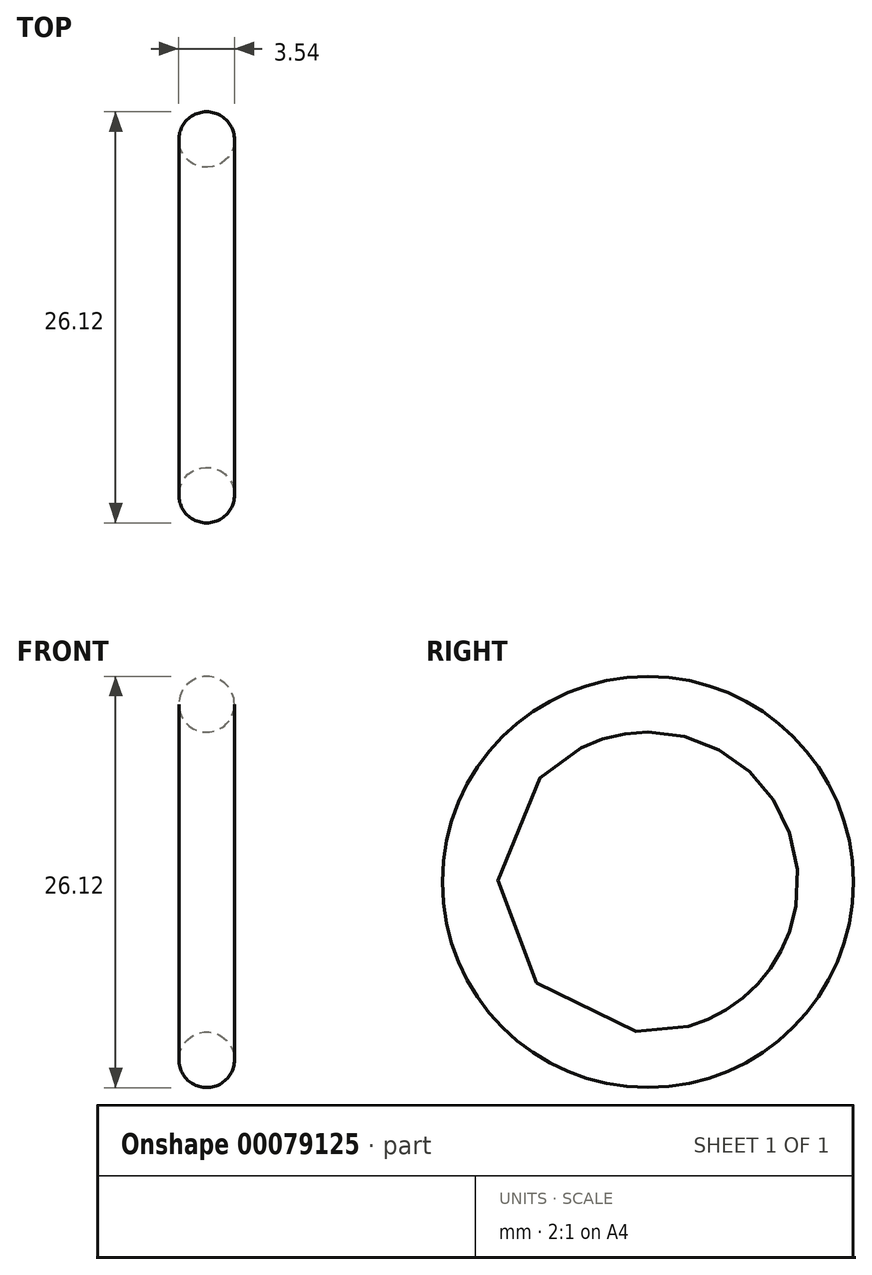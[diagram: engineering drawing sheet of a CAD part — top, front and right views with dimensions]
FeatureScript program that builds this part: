
annotation { "Feature Type Name" : "Feature", "Feature Type Description" : "" }
export const myFeature = defineFeature(function(context is Context, id is Id, definition is map)
    precondition{}
    {
        {
            var Q0;
            Q0=qCreatedBy(makeId("Front.planeOp"),FACE);
            var sketch = newSketch(context, id + "F0", { "sketchPlane" : qUnion([Q0])});
            skLineSegment(sketch, "E0", {"start": v(-17.65, 0) * mm, "end": v(27.96, 0) * mm});
            skCircle(sketch, "E1", {"center": v(0, 11.3) * mm, "radius": 1.77 * mm});
            skSolve(sketch);
        }
        {
            var Q0;
            Q0=makeQuery(id+"F0.imprint","IMPRINT",FACE,{"disambiguationData":[TD([[makeQuery(id+"F0.imprint","IMPRINT",EDGE,{"derivedFrom":sQuery(id+"F0.wireOp",EDGE,"E1")}),1.0]])]});
            var Q1;
            Q1=sQuery(id+"F0.wireOp",EDGE,"E0");
            revolve(context, id + "F1", {"entities" : qUnion([Q0]), "axis" : qUnion([Q1]), "revolveType" : RevolveType.FULL});
        }
    });
